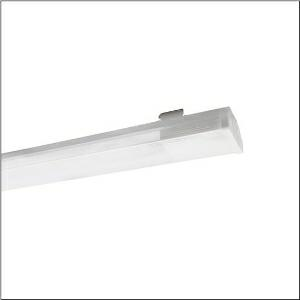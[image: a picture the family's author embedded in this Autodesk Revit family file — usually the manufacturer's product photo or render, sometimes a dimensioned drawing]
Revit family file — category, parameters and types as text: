
# Revit family: modario_r__31_gen_2_53bm8117u4gxc2_3746
name_source: partatom
category: Lighting Fixtures
units: mm (PartAtom-declared; Revit-internal decimal feet)

## family parameters
Cut with Voids When Loaded = No
Host = Face
Light Source = No
Part Type = Normal
Room Calculation Point = No
Round Connector Dimension = Use Diameter
Shared = No

## types (1)
- Modario® 31 Gen.2 (1 x LED, 16360 lm, 90.4 W, 4000K)
    Apparent Load = 90 VA
    CIE Flux Codes = 50 78 94 90 100
    Color Rendering = 80
    Color Temperature = 4000K
    Default Elevation = 1800 mm
    Description = Modario® 31 Gen.2, luminaire insert, of sheet steel, coil coated, white, length: 2.392mm, width: 81mm, height: 82mm, 8x system unit, system units: 299mm, LED rated luminous flux: 16.360lm, light colour: 840, control gear: ON/OFF, with plug, 3-pole, with phase selection, mains connection: 220..240V, AC, 50/60Hz, rated input power: 90W, through-wiring accessed according to module size, primary optical cover: cover, of PMMA, light emission: direct distribution, primary light characteristic: symmetric, protection rating (complete): IP20, protection rating (LED compartment): IP50, insulation class (complete): insulation class I (protective earthing), certification: CE, ENEC, VDE, UKCA, impact resistance: IK03, permissible ambient temperature for indoor applications: -40..+40°C, corresponds to IFS (International Featured Standards) requirements for safety and quality in the food industry, reducing of maximum allowable ambient temperature of 5°C with ceiling mounting, packaging unit: 1 piece
    Height = 92 mm
    Lamp = 1 x LED
    Lamp Light Flux = 16360 lm
    Lamp Power = 90.4 W
    Lamp count = 1
    Length = 2392 mm
    Luminous efficacy = 181 lm/W
    Manufacturer = Siteco
    ModVariant = No
    Model = 53BM8117U4GXC2
    Mounting Place = Ceiling
    Mounting Type = Pendant
    Number of Poles = 1
    OnlyDefault = Yes
    Power Factor = 1
    Product Name = Modario® 31 Gen.2
    Product group = luminaire insert
    ProductGroupID = 902
    Protection Class = Protection class I
    Protection Degree = IP 20
    RLX_Detail_Level = 1
    RLX_Emergency_Light_Flux = 0 lm
    RLX_Emergency_Type = 0
    RLX_Emergency_Type_DB = No
    RlxData = <blob elided: 34645 chars, md5=7308991a>
    Socket = socket
    Standby Power = 0 W
    System Light Flux = 16360 lm
    System Power = 90 W
    Type Comments = Product without accessories
    Type Image = l_1341883.jpg
    URL = http://relux.com
    VarID = ---
    Voltage = 0 V
    Weight = 0.00 kg
    Width = 81 mm

## geometry (parser evidence)
native form markers: Blend x4, Sweep x12
no freeform markers — native parametric forms only
